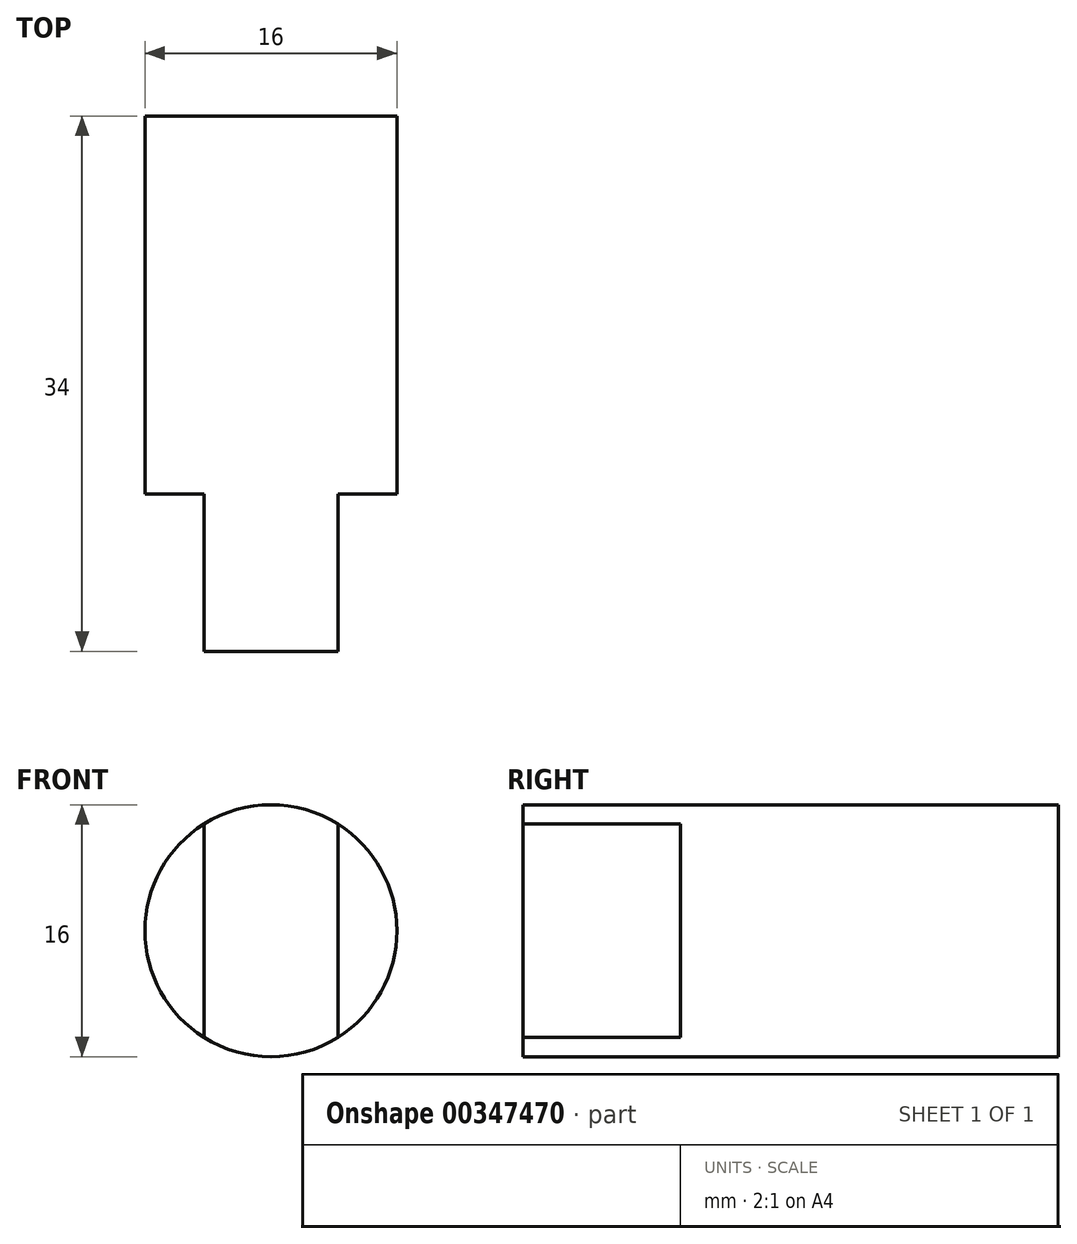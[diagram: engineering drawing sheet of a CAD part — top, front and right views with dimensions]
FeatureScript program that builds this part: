
annotation { "Feature Type Name" : "Feature", "Feature Type Description" : "" }
export const myFeature = defineFeature(function(context is Context, id is Id, definition is map)
    precondition{}
    {
        {
            var Q0;
            Q0=qCreatedBy(makeId("Front.planeOp"),FACE);
            var sketch = newSketch(context, id + "F0", { "sketchPlane" : qUnion([Q0])});
            skCircle(sketch, "E0", {"center": v(0, 0) * mm, "radius": 8 * mm});
            skSolve(sketch);
        }
        {
            var Q0;
            Q0=makeQuery(id+"F0.imprint","IMPRINT",FACE,{"disambiguationData":[TD([[makeQuery(id+"F0.imprint","IMPRINT",EDGE,{"derivedFrom":sQuery(id+"F0.wireOp",EDGE,"E0")}),1.0]])]});
            extrude(context, id + "F1", {"entities" : qUnion([Q0]), "depth" : 24 * mm});
        }
        {
            var Q0;
            Q0=makeQuery(id+"F1.opExtrude","CAP_FACE",FACE,{"disambiguationData":[OSD([sQuery(id+"F0.wireOp",EDGE,"E0")])],"isStart":false});
            var sketch = newSketch(context, id + "F2", { "sketchPlane" : qUnion([Q0])});
            skLineSegment(sketch, "E1", {"start": v(0, 0) * mm, "end": v(4.25, 0) * mm});
            skLineSegment(sketch, "E2", {"start": v(0, 0) * mm, "end": v(-4.25, 0) * mm});
            skLineSegment(sketch, "E3", {"start": v(-4.25, 0) * mm, "end": v(-4.25, -6.78) * mm});
            skLineSegment(sketch, "E4", {"start": v(-4.25, -6.78) * mm, "end": v(-4.25, 6.78) * mm});
            skLineSegment(sketch, "E5", {"start": v(4.25, 0) * mm, "end": v(4.25, -6.78) * mm});
            skLineSegment(sketch, "E6", {"start": v(4.25, -6.78) * mm, "end": v(4.25, 6.78) * mm});
            skSolve(sketch);
        }
        {
            var Q0;
            {var subQ5=sQuery(id+"F2.wireOp",EDGE,"E1");Q0=makeQuery(id+"F2.imprint","IMPRINT",FACE,{"disambiguationData":[TD([[makeQuery(id+"F2.imprint","IMPRINT",EDGE,{"derivedFrom":subQ5}),1.0]])]});}
            var Q1;
            {var subQ1=sQuery(id+"F2.wireOp",EDGE,"E1");Q1=makeQuery(id+"F2.imprint","IMPRINT",FACE,{"disambiguationData":[TD([[makeQuery(id+"F2.imprint","IMPRINT",EDGE,{"derivedFrom":subQ1}),-1.0]])]});}
            extrude(context, id + "F3", {"entities" : qUnion([Q0, Q1]), "operationType" : NewBodyOperationType.ADD, "depth" : 10 * mm});
        }
    });
